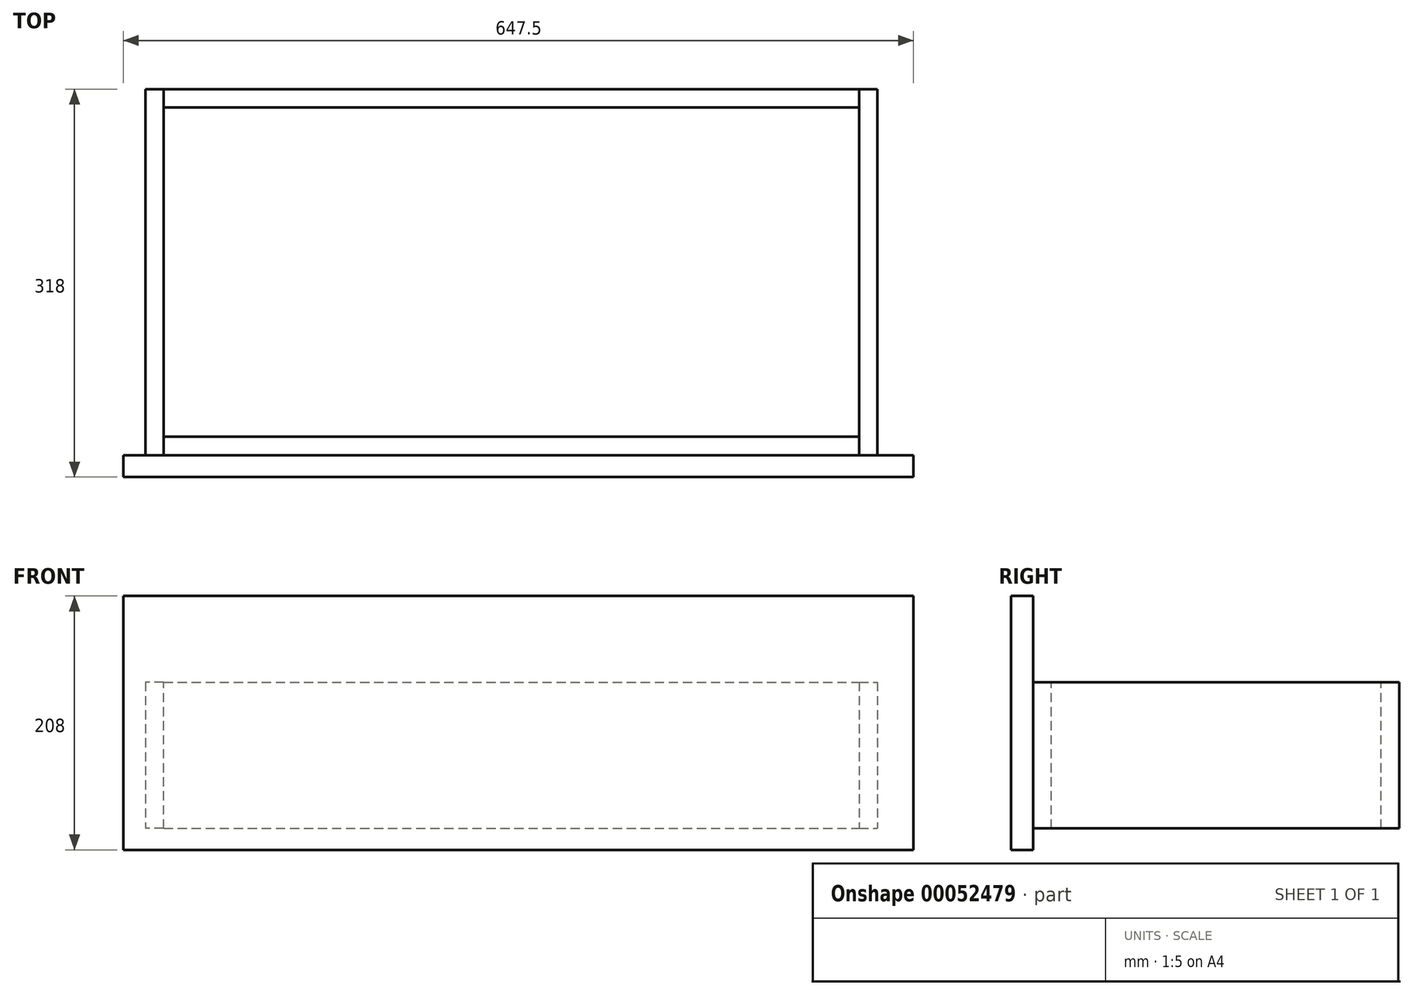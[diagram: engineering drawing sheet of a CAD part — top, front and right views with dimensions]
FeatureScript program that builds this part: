
annotation { "Feature Type Name" : "Feature", "Feature Type Description" : "" }
export const myFeature = defineFeature(function(context is Context, id is Id, definition is map)
    precondition{}
    {
        {
            var Q0;
            Q0=qCreatedBy(makeId("Front.planeOp"),FACE);
            var sketch = newSketch(context, id + "F0", { "sketchPlane" : qUnion([Q0])});
            skLineSegment(sketch, "E0.bottom", {"start": v(-285, 0) * mm, "end": v(285, 0) * mm});
            skLineSegment(sketch, "E0.top", {"start": v(-285, 120) * mm, "end": v(285, 120) * mm});
            skLineSegment(sketch, "E0.left", {"start": v(-285, 0) * mm, "end": v(-285, 120) * mm});
            skLineSegment(sketch, "E0.right", {"start": v(285, 0) * mm, "end": v(285, 120) * mm});
            skSolve(sketch);
        }
        {
            var Q0;
            Q0=makeQuery(id+"F0.imprint","IMPRINT",FACE,{"disambiguationData":[TD([[makeQuery(id+"F0.imprint","IMPRINT",EDGE,{"derivedFrom":sQuery(id+"F0.wireOp",EDGE,"E0.bottom")}),1.0]])]});
            extrude(context, id + "F1", {"entities" : qUnion([Q0]), "depth" : 15 * mm});
        }
        {
            var Q0;
            Q0=makeQuery(id+"F1.opExtrude","CAP_FACE",FACE,{"disambiguationData":[OSD([sQuery(id+"F0.wireOp",EDGE,"E0.bottom"),sQuery(id+"F0.wireOp",EDGE,"E0.top"),sQuery(id+"F0.wireOp",EDGE,"E0.left"),sQuery(id+"F0.wireOp",EDGE,"E0.right")])],"isStart":false});
            var sketch = newSketch(context, id + "F2", { "sketchPlane" : qUnion([Q0])});
            skLineSegment(sketch, "E1.bottom", {"start": v(285, 120) * mm, "end": v(300, 120) * mm});
            skLineSegment(sketch, "E1.top", {"start": v(285, 0) * mm, "end": v(300, 0) * mm});
            skLineSegment(sketch, "E1.left", {"start": v(285, 120) * mm, "end": v(285, 0) * mm});
            skLineSegment(sketch, "E1.right", {"start": v(300, 120) * mm, "end": v(300, 0) * mm});
            skLineSegment(sketch, "E2.bottom", {"start": v(-285, 120) * mm, "end": v(-300, 120) * mm});
            skLineSegment(sketch, "E2.top", {"start": v(-285, 0) * mm, "end": v(-300, 0) * mm});
            skLineSegment(sketch, "E2.left", {"start": v(-285, 120) * mm, "end": v(-285, 0) * mm});
            skLineSegment(sketch, "E2.right", {"start": v(-300, 120) * mm, "end": v(-300, 0) * mm});
            skSolve(sketch);
        }
        {
            var Q0;
            Q0 = qSketchRegion(id + "F2", true);
            extrude(context, id + "F3", {"entities" : qUnion([Q0]), "oppositeDirection" : true, "depth" : 300 * mm});
        }
        {
            var Q0;
            Q0=makeQuery(id+"F3.opExtrude","SWEPT_FACE",FACE,{"disambiguationData":[OSD([sQuery(id+"F2.wireOp",EDGE,"E1.left")])]});
            var sketch = newSketch(context, id + "F4", { "sketchPlane" : qUnion([Q0])});
            skLineSegment(sketch, "E3.bottom", {"start": v(-285, 120) * mm, "end": v(-270, 120) * mm});
            skLineSegment(sketch, "E3.top", {"start": v(-285, 0) * mm, "end": v(-270, 0) * mm});
            skLineSegment(sketch, "E3.left", {"start": v(-285, 120) * mm, "end": v(-285, 0) * mm});
            skLineSegment(sketch, "E3.right", {"start": v(-270, 120) * mm, "end": v(-270, 0) * mm});
            skSolve(sketch);
        }
        {
            var Q0;
            Q0 = qSketchRegion(id + "F4", true);
            extrude(context, id + "F5", {"entities" : qUnion([Q0]), "endBound" : BoundingType.UP_TO_NEXT, "depth" : 25 * mm});
        }
        {
            var Q0;
            Q0=makeQuery(id+"F1.opExtrude","CAP_FACE",FACE,{"disambiguationData":[OSD([sQuery(id+"F0.wireOp",EDGE,"E0.bottom"),sQuery(id+"F0.wireOp",EDGE,"E0.top"),sQuery(id+"F0.wireOp",EDGE,"E0.left"),sQuery(id+"F0.wireOp",EDGE,"E0.right")])],"isStart":false});
            var sketch = newSketch(context, id + "F6", { "sketchPlane" : qUnion([Q0])});
            skLineSegment(sketch, "E4.bottom", {"start": v(-318, 190.5) * mm, "end": v(329.5, 190.5) * mm});
            skLineSegment(sketch, "E4.top", {"start": v(-318, -17.5) * mm, "end": v(329.5, -17.5) * mm});
            skLineSegment(sketch, "E4.left", {"start": v(-318, 190.5) * mm, "end": v(-318, -17.5) * mm});
            skLineSegment(sketch, "E4.right", {"start": v(329.5, 190.5) * mm, "end": v(329.5, -17.5) * mm});
            skPoint(sketch, "E5.startSnap0", {"position": v(5.75, -17.5) * mm});
            skSolve(sketch);
        }
        {
            var Q0;
            Q0 = qSketchRegion(id + "F6", true);
            extrude(context, id + "F7", {"entities" : qUnion([Q0]), "depth" : 18 * mm});
        }
    });
